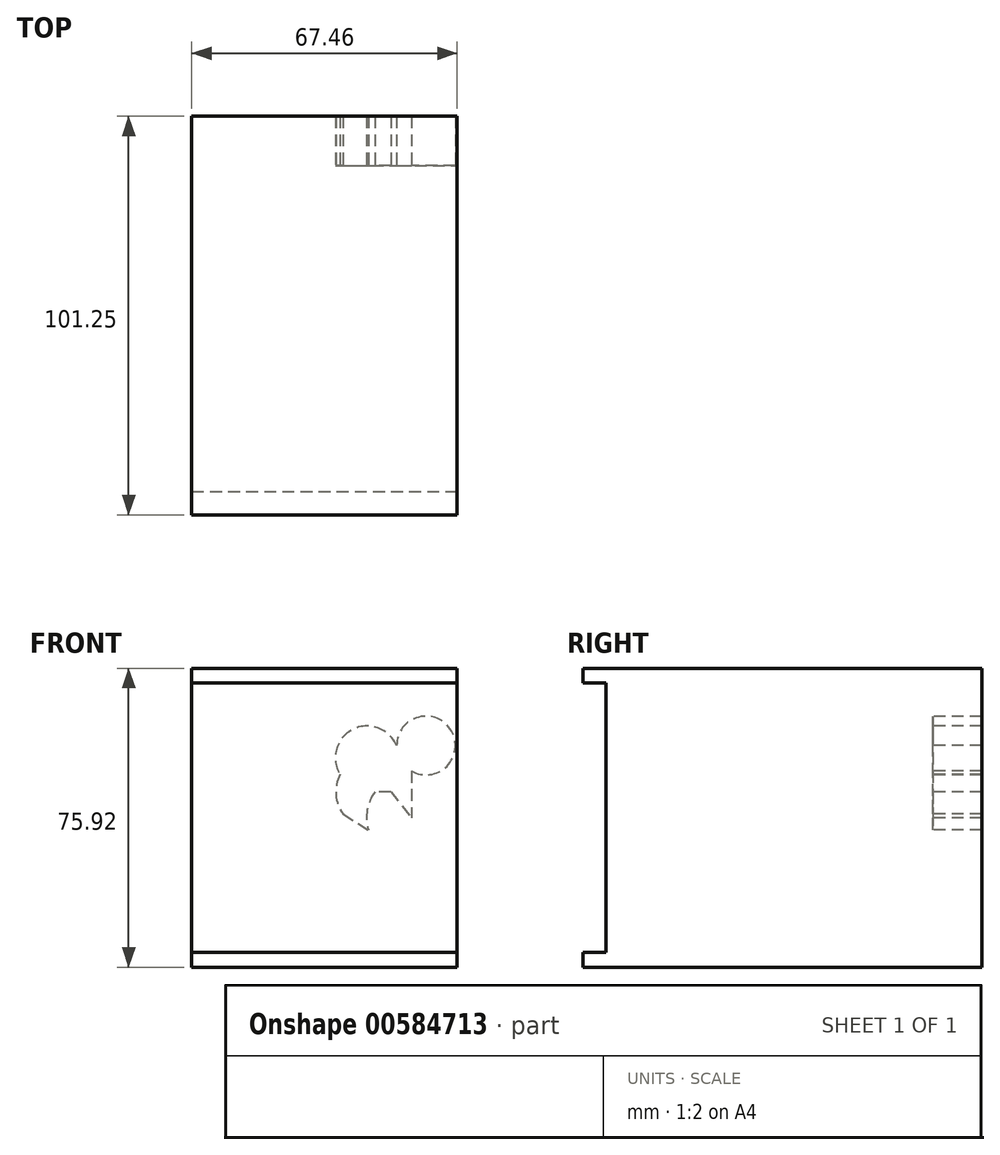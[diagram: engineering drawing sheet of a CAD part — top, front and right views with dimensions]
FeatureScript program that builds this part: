
annotation { "Feature Type Name" : "Feature", "Feature Type Description" : "" }
export const myFeature = defineFeature(function(context is Context, id is Id, definition is map)
    precondition{}
    {
        {
            var Q0;
            Q0=qCreatedBy(makeId("Right.planeOp"),FACE);
            var sketch = newSketch(context, id + "F0", { "sketchPlane" : qUnion([Q0])});
            skLineSegment(sketch, "E0.bottom", {"start": v(0, 34.24) * mm, "end": v(-74.58, 34.24) * mm});
            skLineSegment(sketch, "E0.top", {"start": v(0, -34.24) * mm, "end": v(-74.58, -34.24) * mm});
            skLineSegment(sketch, "E0.left", {"start": v(0, 34.24) * mm, "end": v(0, -34.24) * mm});
            skLineSegment(sketch, "E0.right", {"start": v(-74.58, 34.24) * mm, "end": v(-74.58, -34.24) * mm});
            skPoint(sketch, "E0.middle", {"position": v(-37.3, 0) * mm});
            skLineSegment(sketch, "E1.bottom", {"start": v(76.76, 37.96) * mm, "end": v(-5.8, 37.96) * mm});
            skLineSegment(sketch, "E1.top", {"start": v(76.76, -37.96) * mm, "end": v(-5.8, -37.96) * mm});
            skLineSegment(sketch, "E1.left", {"start": v(76.76, 37.96) * mm, "end": v(76.76, -37.96) * mm});
            skLineSegment(sketch, "E1.right", {"start": v(-5.8, 37.96) * mm, "end": v(-5.8, -37.96) * mm});
            skPoint(sketch, "E1.middle", {"position": v(35.48, 0) * mm});
            skSolve(sketch);
        }
        {
            var Q0;
            {var subQ1=sQuery(id+"F0.wireOp",EDGE,"E0.left");Q0=makeQuery(id+"F0.imprint","IMPRINT",FACE,{"disambiguationData":[TD([[makeQuery(id+"F0.imprint","IMPRINT",EDGE,{"derivedFrom":subQ1}),1.0]])]});}
            extrude(context, id + "F1", {"entities" : qUnion([Q0]), "depth" : 67.46 * mm, "offsetDistance" : 25.4 * mm});
        }
        {
            var Q0;
            Q0=makeQuery(id+"F1.opExtrude","SWEPT_FACE",FACE,{"disambiguationData":[OSD([sQuery(id+"F0.wireOp",EDGE,"E1.left")])]});
            extrude(context, id + "F2", {"entities" : qUnion([Q0]), "operationType" : NewBodyOperationType.ADD, "depth" : 6.22 * mm, "offsetDistance" : 25.4 * mm});
        }
        {
            var Q0;
            Q0=makeQuery(id+"F2.opExtrude","CAP_FACE",FACE,{"disambiguationData":[OSD([sQuery(id+"F0.wireOp",EDGE,"E1.left")])],"isStart":false});
            var sketch = newSketch(context, id + "F3", { "sketchPlane" : qUnion([Q0])});
            skArc(sketch, "E2", {"start": v(-37.67, 10.97) * mm, "mid": v(-36.66, 5.86) * mm, "end": v(-38.39, 0.95) * mm});
            skArc(sketch, "E3", {"start": v(-37.67, 10.97) * mm, "mid": v(-40.9, 22.41) * mm, "end": v(-52.08, 18.34) * mm});
            skArc(sketch, "E4", {"start": v(-52.08, 18.34) * mm, "mid": v(-66, 22.07) * mm, "end": v(-55.8, 11.9) * mm});
            skArc(sketch, "E5", {"start": v(-46.52, 6.57) * mm, "mid": v(-44.6, 1.93) * mm, "end": v(-44.86, -3.08) * mm});
            skLineSegment(sketch, "E6", {"start": v(-38.39, 0.95) * mm, "end": v(-44.86, -3.08) * mm});
            skLineSegment(sketch, "E7", {"start": v(-50.58, 6.57) * mm, "end": v(-46.52, 6.57) * mm});
            skLineSegment(sketch, "E8", {"start": v(-55.8, 11.9) * mm, "end": v(-55.8, 0) * mm});
            skLineSegment(sketch, "E9", {"start": v(-50.58, 6.57) * mm, "end": v(-55.8, 0) * mm});
            skSolve(sketch);
        }
        {
            var Q0;
            Q0=makeQuery(id+"F3.imprint","IMPRINT",FACE,{"disambiguationData":[TD([[makeQuery(id+"F3.imprint","IMPRINT",EDGE,{"derivedFrom":sQuery(id+"F3.wireOp",EDGE,"E2")}),-1.0]])]});
            extrude(context, id + "F4", {"entities" : qUnion([Q0]), "operationType" : NewBodyOperationType.ADD, "depth" : 12.46 * mm, "offsetDistance" : 25.4 * mm});
        }
    });
